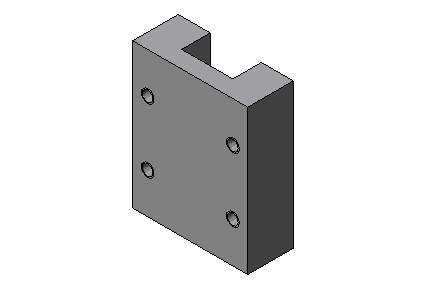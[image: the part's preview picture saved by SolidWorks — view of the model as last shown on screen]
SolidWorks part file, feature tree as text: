
SOLIDWORKS PART (.sldprt)
format: sldprt  version: not decoded by parser v0  size: 159,232 bytes
history: native  units: mm
features: sketch x4, thread x4, extrude x1, cut_extrude x1, hole x1 (+10 scaffold rows collapsed)
feature tree (21):
  scaffold x10  (default folders/planes/origin — collapsed)
  sketch  "Sketch1"  dims[D1=27.0mm D2=10.7mm]
  extrude  "Extrude1"  Depth=34mm
  sketch  "Sketch2"  dims[D1=12.0mm D2=6.7mm]
  cut_extrude  "Cut-Extrude1"  [1 undecoded]
  hole  "M3x0.5 Tapped Hole1"  Diameter=2.5mm Depth=7.499985mm
  sketch  "Sketch4"  dims[D1=20.0mm D2=15.0mm]
  sketch  "Sketch3"  dims[hole-wizard template sketch: 47 standard entries collapsed; hole parameters kept: c15.Tap Drill Depth=~7.499985mm c15.D3=~14.816244mm c15.Drill Angle=118.0deg]
  thread  "Cosmetic Thread1"  Diameter=5.999988mm  [1 undecoded]
  thread  "Cosmetic Thread2"  Diameter=5.999988mm  [1 undecoded]
  thread  "Cosmetic Thread3"  Diameter=5.999988mm  [1 undecoded]
  thread  "Cosmetic Thread4"  Diameter=5.999988mm  [1 undecoded]
decode coverage: 10 of 11 modeling features carry decoded parameters
note: ~ marks probable driven/reference dimensions
note: 5 parameter values undecoded
note: suppression state not decoded; provenance and decode notes live in map.json
